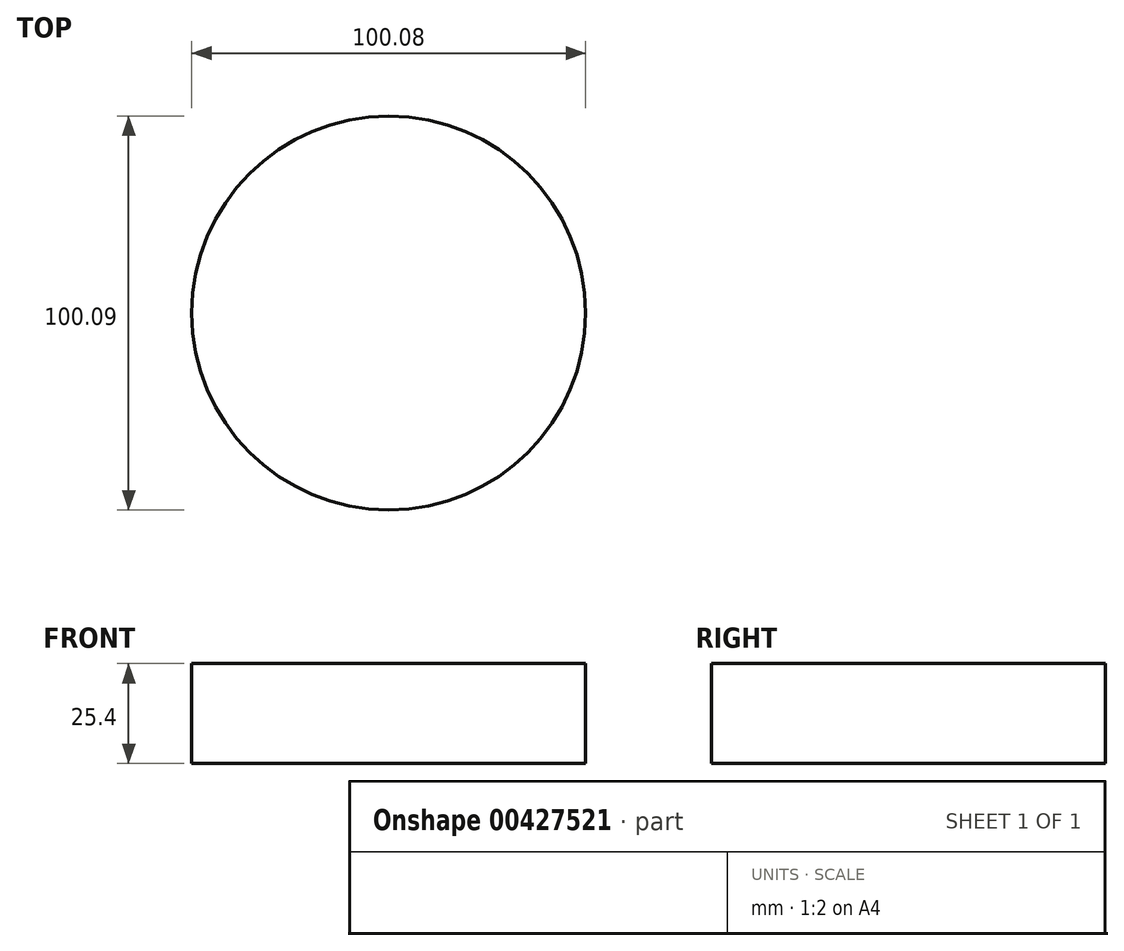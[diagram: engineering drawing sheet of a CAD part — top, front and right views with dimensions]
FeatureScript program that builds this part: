
annotation { "Feature Type Name" : "Feature", "Feature Type Description" : "" }
export const myFeature = defineFeature(function(context is Context, id is Id, definition is map)
    precondition{}
    {
        {
            var Q0;
            Q0=qCreatedBy(makeId("Top.planeOp"),FACE);
            var sketch = newSketch(context, id + "F0", { "sketchPlane" : qUnion([Q0])});
            skCircle(sketch, "E0", {"center": v(-38.34, -65.89) * mm, "radius": 50.04 * mm});
            skSolve(sketch);
        }
        {
            var Q0;
            Q0=makeQuery(id+"F0.imprint","IMPRINT",FACE,{"disambiguationData":[TD([[makeQuery(id+"F0.imprint","IMPRINT",EDGE,{"derivedFrom":sQuery(id+"F0.wireOp",EDGE,"E0")}),1.0]])]});
            extrude(context, id + "F1", {"entities" : qUnion([Q0]), "depth" : 25.4 * mm});
        }
    });
